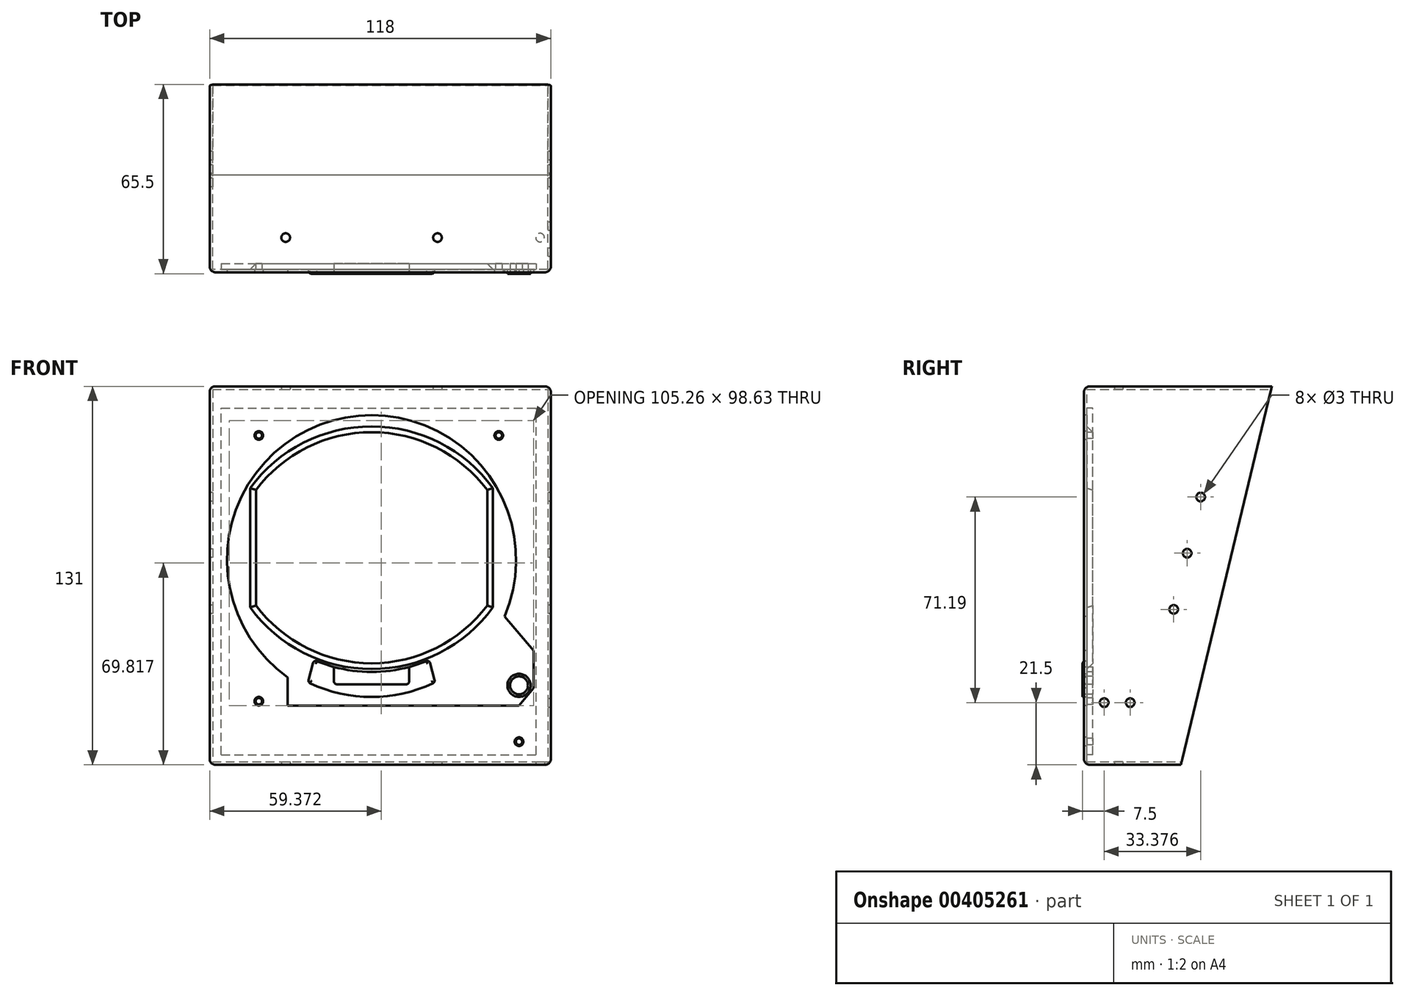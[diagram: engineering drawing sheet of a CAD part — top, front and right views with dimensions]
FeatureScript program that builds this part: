
annotation { "Feature Type Name" : "Feature", "Feature Type Description" : "" }
export const myFeature = defineFeature(function(context is Context, id is Id, definition is map)
    precondition{}
    {
        {
            var Q0;
            Q0=qCreatedBy(makeId("Front.planeOp"),FACE);
            var sketch = newSketch(context, id + "F0", { "sketchPlane" : qUnion([Q0])});
            skLineSegment(sketch, "E0.bottom", {"start": v(-52.84, -65.5) * mm, "end": v(-170.84, -65.5) * mm});
            skLineSegment(sketch, "E0.top", {"start": v(-52.84, 65.5) * mm, "end": v(-170.84, 65.5) * mm});
            skLineSegment(sketch, "E0.left", {"start": v(-52.84, -65.5) * mm, "end": v(-52.84, 65.5) * mm});
            skLineSegment(sketch, "E0.right", {"start": v(-170.84, -65.5) * mm, "end": v(-170.84, 65.5) * mm});
            skPoint(sketch, "E0.middle", {"position": v(-111.84, 0) * mm});
            skSolve(sketch);
        }
        {
            var Q0;
            Q0=makeQuery(id+"F0.imprint","IMPRINT",FACE,{"disambiguationData":[TD([[makeQuery(id+"F0.imprint","IMPRINT",EDGE,{"derivedFrom":sQuery(id+"F0.wireOp",EDGE,"E0.bottom")}),-1.0]])]});
            extrude(context, id + "F1", {"entities" : qUnion([Q0]), "endBound" : BoundingType.SYMMETRIC, "depth" : 120 * mm});
        }
        {
            var Q0;
            Q0=makeQuery(id+"F1.opExtrude","CAP_FACE",FACE,{"disambiguationData":[OSD([sQuery(id+"F0.wireOp",EDGE,"E0.bottom"),sQuery(id+"F0.wireOp",EDGE,"E0.top"),sQuery(id+"F0.wireOp",EDGE,"E0.left"),sQuery(id+"F0.wireOp",EDGE,"E0.right")])],"isStart":true});
            shell(context, id + "F2", {"entities" : qUnion([Q0]), "thickness" : 1 * mm});
        }
        {
            var Q0;
            Q0=makeQuery(id+"F1.opExtrude","SWEPT_FACE",FACE,{"disambiguationData":[OSD([sQuery(id+"F0.wireOp",EDGE,"E0.right")])]});
            var sketch = newSketch(context, id + "F3", { "sketchPlane" : qUnion([Q0])});
            skLineSegment(sketch, "E1", {"start": v(-5, 65.5) * mm, "end": v(26.45, -65.5) * mm});
            skLineSegment(sketch, "E2", {"start": v(26.45, -65.5) * mm, "end": v(-89.83, -65.5) * mm});
            skLineSegment(sketch, "E3", {"start": v(-89.83, -65.5) * mm, "end": v(-89.83, 65.5) * mm});
            skLineSegment(sketch, "E4", {"start": v(-89.83, 65.5) * mm, "end": v(-5, 65.5) * mm});
            skCircle(sketch, "E5", {"center": v(19.62, 27.19) * mm, "radius": 1.5 * mm});
            skCircle(sketch, "E6", {"center": v(28.96, -11.7) * mm, "radius": 1.5 * mm});
            skLineSegment(sketch, "E7", {"start": v(9.7, 4.24) * mm, "end": v(48.51, 13.56) * mm, "construction": true});
            skLineSegment(sketch, "E8", {"start": v(4.8, 24.66) * mm, "end": v(14.6, -16.18) * mm, "construction": true});
            skLineSegment(sketch, "E9", {"start": v(14.6, -16.18) * mm, "end": v(16.55, -15.71) * mm, "construction": true});
            skLineSegment(sketch, "E10", {"start": v(16.55, -15.71) * mm, "end": v(6.75, 25.13) * mm, "construction": true});
            skLineSegment(sketch, "E11", {"start": v(6.75, 25.13) * mm, "end": v(4.8, 24.66) * mm, "construction": true});
            skCircle(sketch, "E12", {"center": v(24.3, 7.74) * mm, "radius": 1.5 * mm});
            skSolve(sketch);
        }
        {
            var Q0;
            Q0=qSketchRegion(id+"F3",true);
            extrude(context, id + "F4", {"entities" : qUnion([Q0]), "operationType" : NewBodyOperationType.REMOVE, "oppositeDirection" : true, "depth" : 150 * mm});
        }
        {
            var Q0;
            Q0=makeQuery(id+"F1.opExtrude","CAP_EDGE",EDGE,{"disambiguationData":[OSD([sQuery(id+"F0.wireOp",EDGE,"E0.right")])],"isStart":false});
            var Q1;
            Q1=makeQuery(id+"F1.opExtrude","SWEPT_EDGE",EDGE,{"disambiguationData":[OSD([sQuery(id+"F0.wireOp",EDGE,"E0.top"),sQuery(id+"F0.wireOp",EDGE,"E0.right")])]});
            var Q2;
            Q2=makeQuery(id+"F1.opExtrude","CAP_EDGE",EDGE,{"disambiguationData":[OSD([sQuery(id+"F0.wireOp",EDGE,"E0.top")])],"isStart":false});
            var Q3;
            Q3=makeQuery(id+"F1.opExtrude","CAP_EDGE",EDGE,{"disambiguationData":[OSD([sQuery(id+"F0.wireOp",EDGE,"E0.left")])],"isStart":false});
            var Q4;
            Q4=makeQuery(id+"F1.opExtrude","SWEPT_EDGE",EDGE,{"disambiguationData":[OSD([sQuery(id+"F0.wireOp",EDGE,"E0.top"),sQuery(id+"F0.wireOp",EDGE,"E0.left")])]});
            var Q5;
            Q5=makeQuery(id+"F1.opExtrude","CAP_EDGE",EDGE,{"disambiguationData":[OSD([sQuery(id+"F0.wireOp",EDGE,"E0.bottom")])],"isStart":false});
            var Q6;
            Q6=makeQuery(id+"F1.opExtrude","SWEPT_EDGE",EDGE,{"disambiguationData":[OSD([sQuery(id+"F0.wireOp",EDGE,"E0.bottom"),sQuery(id+"F0.wireOp",EDGE,"E0.left")])]});
            var Q7;
            Q7=makeQuery(id+"F1.opExtrude","SWEPT_EDGE",EDGE,{"disambiguationData":[OSD([sQuery(id+"F0.wireOp",EDGE,"E0.bottom"),sQuery(id+"F0.wireOp",EDGE,"E0.right")])]});
            fillet(context, id + "F5", {"entities" : qUnion([Q0, Q1, Q2, Q3, Q4, Q5, Q6, Q7]), "radius" : 2 * mm, "tangentPropagation" : true, "allowEdgeOverflow" : false});
        }
        {
            var Q0;
            Q0=makeQuery(id+"F1.opExtrude","CAP_FACE",FACE,{"disambiguationData":[OSD([sQuery(id+"F0.wireOp",EDGE,"E0.bottom"),sQuery(id+"F0.wireOp",EDGE,"E0.top"),sQuery(id+"F0.wireOp",EDGE,"E0.left"),sQuery(id+"F0.wireOp",EDGE,"E0.right")])],"isStart":false});
            var sketch = newSketch(context, id + "F6", { "sketchPlane" : qUnion([Q0])});
            skCircle(sketch, "E13", {"center": v(-114.84, 5.5) * mm, "radius": 50 * mm});
            skLineSegment(sketch, "E14", {"start": v(-143.84, -35.23) * mm, "end": v(-143.84, -45) * mm});
            skLineSegment(sketch, "E15", {"start": v(-143.84, -45) * mm, "end": v(-63.84, -45) * mm});
            skLineSegment(sketch, "E16", {"start": v(-63.84, -45) * mm, "end": v(-58.84, -39) * mm});
            skLineSegment(sketch, "E17", {"start": v(-58.84, -39) * mm, "end": v(-58.84, -26) * mm});
            skLineSegment(sketch, "E18", {"start": v(-58.84, -26) * mm, "end": v(-68.86, -14.15) * mm});
            skCircle(sketch, "E19", {"center": v(-153.84, 48.5) * mm, "radius": 1.5 * mm});
            skCircle(sketch, "E20", {"center": v(-70.84, 48.5) * mm, "radius": 1.5 * mm});
            skCircle(sketch, "E21", {"center": v(-153.84, -43.5) * mm, "radius": 1.5 * mm});
            skCircle(sketch, "E22", {"center": v(-63.84, -57.5) * mm, "radius": 1.5 * mm});
            skSolve(sketch);
        }
        {
            var Q0;
            Q0=qSketchRegion(id+"F6",true);
            extrude(context, id + "F7", {"entities" : qUnion([Q0]), "operationType" : NewBodyOperationType.REMOVE, "oppositeDirection" : true, "depth" : 1 * mm});
        }
        {
            var Q0;
            Q0=makeQuery(id+"F2.opShell","OFFSET_FACE",FACE,{"disambiguationData":[OSD([sQuery(id+"F0.wireOp",EDGE,"E0.bottom"),sQuery(id+"F0.wireOp",EDGE,"E0.top"),sQuery(id+"F0.wireOp",EDGE,"E0.left"),sQuery(id+"F0.wireOp",EDGE,"E0.right")])]});
            var sketch = newSketch(context, id + "F8", { "sketchPlane" : qUnion([Q0])});
            skLineSegment(sketch, "E23.bottom", {"start": v(166.84, -62) * mm, "end": v(57.84, -62) * mm});
            skLineSegment(sketch, "E23.top", {"start": v(166.84, 58) * mm, "end": v(57.84, 58) * mm});
            skLineSegment(sketch, "E23.left", {"start": v(166.84, -62) * mm, "end": v(166.84, 58) * mm});
            skLineSegment(sketch, "E23.right", {"start": v(57.84, -62) * mm, "end": v(57.84, 58) * mm});
            skPoint(sketch, "E23.middle", {"position": v(114.84, 5.5) * mm});
            skCircle(sketch, "E24", {"center": v(153.84, 48.5) * mm, "radius": 1.1 * mm});
            skCircle(sketch, "E25", {"center": v(70.84, 48.5) * mm, "radius": 1.1 * mm});
            skCircle(sketch, "E26", {"center": v(63.84, -57.5) * mm, "radius": 1.1 * mm});
            skCircle(sketch, "E27", {"center": v(153.84, -43.5) * mm, "radius": 1.1 * mm});
            skCircle(sketch, "E28", {"center": v(63.84, -38) * mm, "radius": 3.1 * mm});
            skLineSegment(sketch, "E29.bottom", {"start": v(74.84, -10.37) * mm, "end": v(154.84, -10.37) * mm, "construction": true});
            skLineSegment(sketch, "E29.top", {"start": v(74.84, 29.63) * mm, "end": v(154.84, 29.63) * mm, "construction": true});
            skLineSegment(sketch, "E29.left", {"start": v(74.84, -10.37) * mm, "end": v(74.84, 29.63) * mm});
            skLineSegment(sketch, "E29.right", {"start": v(154.84, -10.37) * mm, "end": v(154.84, 29.63) * mm});
            skPoint(sketch, "E29.middle", {"position": v(114.84, 9.63) * mm});
            skArc(sketch, "E30", {"start": v(154.84, 29.63) * mm, "mid": v(114.84, 49.63) * mm, "end": v(74.84, 29.63) * mm});
            skArc(sketch, "E31", {"start": v(74.84, -10.37) * mm, "mid": v(114.84, -30.37) * mm, "end": v(154.84, -10.37) * mm});
            skSolve(sketch);
        }
        {
            var Q0;
            Q0=qSketchRegion(id+"F8",true);
            extrude(context, id + "F9", {"entities" : qUnion([Q0]), "depth" : 2 * mm});
        }
        {
            var Q0;
            Q0=makeQuery(id+"F9.opExtrude","CAP_FACE",FACE,{"disambiguationData":[OSD([sQuery(id+"F8.wireOp",EDGE,"E23.bottom"),sQuery(id+"F8.wireOp",EDGE,"E23.top"),sQuery(id+"F8.wireOp",EDGE,"E23.left"),sQuery(id+"F8.wireOp",EDGE,"E23.right"),sQuery(id+"F8.wireOp",EDGE,"E24"),sQuery(id+"F8.wireOp",EDGE,"E25"),sQuery(id+"F8.wireOp",EDGE,"E26"),sQuery(id+"F8.wireOp",EDGE,"E27"),sQuery(id+"F8.wireOp",EDGE,"E28"),sQuery(id+"F8.wireOp",EDGE,"E29.left"),sQuery(id+"F8.wireOp",EDGE,"E29.right"),sQuery(id+"F8.wireOp",EDGE,"E30"),sQuery(id+"F8.wireOp",EDGE,"E31")])],"isStart":true});
            var sketch = newSketch(context, id + "F10", { "sketchPlane" : qUnion([Q0])});
            skArc(sketch, "E32", {"start": v(-134.84, -29.2) * mm, "mid": v(-114.84, -33.37) * mm, "end": v(-94.84, -29.2) * mm});
            skPoint(sketch, "E33", {"position": v(-114.84, -30.37) * mm});
            skArc(sketch, "E34", {"start": v(-136.84, -36.94) * mm, "mid": v(-114.84, -42.04) * mm, "end": v(-92.84, -36.94) * mm});
            skLineSegment(sketch, "E35", {"start": v(-134.84, -29.2) * mm, "end": v(-136.84, -36.94) * mm});
            skLineSegment(sketch, "E36", {"start": v(-94.84, -29.2) * mm, "end": v(-92.84, -36.94) * mm});
            skCircle(sketch, "E37", {"center": v(-63.84, -38) * mm, "radius": 4 * mm});
            skCircle(sketch, "E38", {"center": v(-63.84, -38) * mm, "radius": 3.1 * mm});
            skSolve(sketch);
        }
        {
            var Q0;
            Q0=qSketchRegion(id+"F10",true);
            extrude(context, id + "F11", {"entities" : qUnion([Q0]), "operationType" : NewBodyOperationType.ADD, "depth" : 1.5 * mm});
        }
        {
            var Q0;
            Q0=makeQuery(id+"F11.opExtrude","CAP_FACE",FACE,{"disambiguationData":[OSD([sQuery(id+"F10.wireOp",EDGE,"E32"),sQuery(id+"F10.wireOp",EDGE,"E34"),sQuery(id+"F10.wireOp",EDGE,"E35"),sQuery(id+"F10.wireOp",EDGE,"E36")])],"isStart":false});
            var sketch = newSketch(context, id + "F12", { "sketchPlane" : qUnion([Q0])});
            skLineSegment(sketch, "E39", {"start": v(-127.84, -31.65) * mm, "end": v(-127.84, -37.65) * mm});
            skLineSegment(sketch, "E40", {"start": v(-127.84, -37.65) * mm, "end": v(-101.84, -37.65) * mm});
            skLineSegment(sketch, "E41", {"start": v(-101.84, -37.65) * mm, "end": v(-101.84, -31.65) * mm});
            skArc(sketch, "E42", {"start": v(-127.84, -31.65) * mm, "mid": v(-114.84, -33.37) * mm, "end": v(-101.84, -31.65) * mm});
            skSolve(sketch);
        }
        {
            var Q0;
            Q0=qSketchRegion(id+"F12",true);
            extrude(context, id + "F13", {"entities" : qUnion([Q0]), "operationType" : NewBodyOperationType.REMOVE, "oppositeDirection" : true, "depth" : 25 * mm});
        }
        {
            var Q0;
            Q0=makeQuery(id+"F11.opExtrude","CAP_EDGE",EDGE,{"disambiguationData":[OSD([sQuery(id+"F10.wireOp",EDGE,"E35")])],"isStart":false});
            var Q1;
            Q1=makeQuery(id+"F11.opExtrude","CAP_EDGE",EDGE,{"disambiguationData":[OSD([sQuery(id+"F10.wireOp",EDGE,"E34")])],"isStart":false});
            var Q2;
            {var subQ0=sQuery(id+"F10.wireOp",EDGE,"E32");var subQ1=sQuery(id+"F10.wireOp",EDGE,"E35");Q2=makeQuery(id+"F13.boolean.opBoolean","SPLIT",EDGE,{"disambiguationData":[TD([makeQuery(id+"F11.opExtrude","SWEPT_FACE",FACE,{"disambiguationData":[OSD([subQ1])]})])],"derivedFrom":makeQuery(id+"F11.opExtrude","CAP_EDGE",EDGE,{"disambiguationData":[OSD([subQ0])],"isStart":false})});}
            var Q3;
            Q3=makeQuery(id+"F11.opExtrude","CAP_EDGE",EDGE,{"disambiguationData":[OSD([sQuery(id+"F10.wireOp",EDGE,"E36")])],"isStart":false});
            var Q4;
            {var subQ0=sQuery(id+"F10.wireOp",EDGE,"E32");var subQ1=sQuery(id+"F10.wireOp",EDGE,"E36");Q4=makeQuery(id+"F13.boolean.opBoolean","SPLIT",EDGE,{"disambiguationData":[TD([makeQuery(id+"F11.opExtrude","SWEPT_FACE",FACE,{"disambiguationData":[OSD([subQ1])]})])],"derivedFrom":makeQuery(id+"F11.opExtrude","CAP_EDGE",EDGE,{"disambiguationData":[OSD([subQ0])],"isStart":false})});}
            fillet(context, id + "F14", {"entities" : qUnion([Q0, Q1, Q2, Q3, Q4]), "radius" : 1 * mm, "tangentPropagation" : true, "allowEdgeOverflow" : false});
        }
        {
            var Q0;
            Q0=makeQuery(id+"F14.opFillet","BLEND_EDGE",EDGE,{"blendedFrom":[makeQuery(id+"F11.opExtrude","CAP_EDGE",EDGE,{"disambiguationData":[OSD([sQuery(id+"F10.wireOp",EDGE,"E34")])],"isStart":false}),makeQuery(id+"F11.opExtrude","CAP_EDGE",EDGE,{"disambiguationData":[OSD([sQuery(id+"F10.wireOp",EDGE,"E35")])],"isStart":false})],"blendedInto":[]});
            var Q1;
            {var subQ0=sQuery(id+"F10.wireOp",EDGE,"E32");var subQ1=sQuery(id+"F10.wireOp",EDGE,"E35");Q1=makeQuery(id+"F14.opFillet","BLEND_EDGE",EDGE,{"blendedFrom":[makeQuery(id+"F11.opExtrude","CAP_EDGE",EDGE,{"disambiguationData":[OSD([subQ1])],"isStart":false}),makeQuery(id+"F13.boolean.opBoolean","SPLIT",EDGE,{"disambiguationData":[TD([makeQuery(id+"F11.opExtrude","SWEPT_FACE",FACE,{"disambiguationData":[OSD([subQ1])]})])],"derivedFrom":makeQuery(id+"F11.opExtrude","CAP_EDGE",EDGE,{"disambiguationData":[OSD([subQ0])],"isStart":false})})],"blendedInto":[]});}
            var Q2;
            {var subQ0=sQuery(id+"F10.wireOp",EDGE,"E32");var subQ1=sQuery(id+"F10.wireOp",EDGE,"E36");Q2=makeQuery(id+"F14.opFillet","BLEND_EDGE",EDGE,{"blendedFrom":[makeQuery(id+"F11.opExtrude","CAP_EDGE",EDGE,{"disambiguationData":[OSD([subQ1])],"isStart":false}),makeQuery(id+"F13.boolean.opBoolean","SPLIT",EDGE,{"disambiguationData":[TD([makeQuery(id+"F11.opExtrude","SWEPT_FACE",FACE,{"disambiguationData":[OSD([subQ1])]})])],"derivedFrom":makeQuery(id+"F11.opExtrude","CAP_EDGE",EDGE,{"disambiguationData":[OSD([subQ0])],"isStart":false})})],"blendedInto":[]});}
            var Q3;
            Q3=makeQuery(id+"F14.opFillet","BLEND_EDGE",EDGE,{"blendedFrom":[makeQuery(id+"F11.opExtrude","CAP_EDGE",EDGE,{"disambiguationData":[OSD([sQuery(id+"F10.wireOp",EDGE,"E34")])],"isStart":false}),makeQuery(id+"F11.opExtrude","CAP_EDGE",EDGE,{"disambiguationData":[OSD([sQuery(id+"F10.wireOp",EDGE,"E36")])],"isStart":false})],"blendedInto":[]});
            var Q4;
            Q4=makeQuery(id+"F13.boolean.opBoolean","COPY",EDGE,{"derivedFrom":makeQuery(id+"F13.opExtrude","SWEPT_EDGE",EDGE,{"disambiguationData":[OSD([sQuery(id+"F12.wireOp",EDGE,"E39"),sQuery(id+"F12.wireOp",EDGE,"E40")])]})});
            var Q5;
            Q5=makeQuery(id+"F13.boolean.opBoolean","COPY",EDGE,{"derivedFrom":makeQuery(id+"F13.opExtrude","SWEPT_EDGE",EDGE,{"disambiguationData":[OSD([sQuery(id+"F12.wireOp",EDGE,"E40"),sQuery(id+"F12.wireOp",EDGE,"E41")])]})});
            fillet(context, id + "F15", {"entities" : qUnion([Q0, Q1, Q2, Q3, Q4, Q5]), "radius" : 1 * mm, "tangentPropagation" : true, "allowEdgeOverflow" : false});
        }
        {
            var Q0;
            Q0=makeQuery(id+"F9.opExtrude","CAP_EDGE",EDGE,{"disambiguationData":[OSD([sQuery(id+"F8.wireOp",EDGE,"E29.right")])],"isStart":true});
            var Q1;
            Q1=makeQuery(id+"F9.opExtrude","CAP_EDGE",EDGE,{"disambiguationData":[OSD([sQuery(id+"F8.wireOp",EDGE,"E30")])],"isStart":true});
            var Q2;
            Q2=makeQuery(id+"F9.opExtrude","CAP_EDGE",EDGE,{"disambiguationData":[OSD([sQuery(id+"F8.wireOp",EDGE,"E29.left")])],"isStart":true});
            var Q3;
            Q3=makeQuery(id+"F9.opExtrude","CAP_EDGE",EDGE,{"disambiguationData":[OSD([sQuery(id+"F8.wireOp",EDGE,"E31")])],"isStart":true});
            chamfer(context, id + "F16", {"entities" : qUnion([Q0, Q1, Q2, Q3]), "width" : 2 * mm, "tangentPropagation" : true});
        }
        {
            var Q0;
            Q0=makeQuery(id+"F1.opExtrude","SWEPT_FACE",FACE,{"disambiguationData":[OSD([sQuery(id+"F0.wireOp",EDGE,"E0.bottom")])]});
            var sketch = newSketch(context, id + "F17", { "sketchPlane" : qUnion([Q0])});
            skCircle(sketch, "E43", {"center": v(-144.54, 48) * mm, "radius": 1.5 * mm});
            skCircle(sketch, "E44", {"center": v(-92.04, 48) * mm, "radius": 1.5 * mm});
            skCircle(sketch, "E45", {"center": v(-56.54, 48) * mm, "radius": 1.5 * mm, "construction": true});
            skSolve(sketch);
        }
        {
            var Q0;
            Q0=qSketchRegion(id+"F17",true);
            extrude(context, id + "F18", {"entities" : qUnion([Q0]), "operationType" : NewBodyOperationType.REMOVE, "endBound" : BoundingType.THROUGH_ALL, "oppositeDirection" : true, "depth" : 25 * mm});
        }
        {
            var Q0;
            Q0=makeQuery(id+"F1.opExtrude","SWEPT_FACE",FACE,{"disambiguationData":[OSD([sQuery(id+"F0.wireOp",EDGE,"E0.left")])]});
            var sketch = newSketch(context, id + "F19", { "sketchPlane" : qUnion([Q0])});
            skCircle(sketch, "E46", {"center": v(-53, -44) * mm, "radius": 1.5 * mm});
            skCircle(sketch, "E47", {"center": v(-44, -44) * mm, "radius": 1.5 * mm});
            skSolve(sketch);
        }
        {
            var Q0;
            Q0=qSketchRegion(id+"F19",true);
            extrude(context, id + "F20", {"entities" : qUnion([Q0]), "operationType" : NewBodyOperationType.REMOVE, "oppositeDirection" : true, "depth" : 2 * mm});
        }
        {
            var Q0;
            Q0=makeQuery(id+"F1.opExtrude","SWEPT_FACE",FACE,{"disambiguationData":[OSD([sQuery(id+"F0.wireOp",EDGE,"E0.bottom")])]});
            var sketch = newSketch(context, id + "F21", { "sketchPlane" : qUnion([Q0])});
            skCircle(sketch, "E48", {"center": v(-56.54, 48) * mm, "radius": 1.5 * mm});
            skSolve(sketch);
        }
        {
            var Q0;
            Q0=qSketchRegion(id+"F21",true);
            extrude(context, id + "F22", {"entities" : qUnion([Q0]), "operationType" : NewBodyOperationType.REMOVE, "oppositeDirection" : true, "depth" : 2 * mm});
        }
    });
